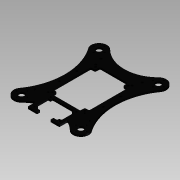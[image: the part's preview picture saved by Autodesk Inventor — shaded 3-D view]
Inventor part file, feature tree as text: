
AUTODESK INVENTOR PART (.ipt)
format: ipt  version: 2015 SP1 (Build 190203100, 203)  size: 542,208 bytes
history: native  units: mm
features: sketch x13, extrude x8, reference x2, projected_geometry x2
ambient origin geometry x8: Origin, YZ Plane, XZ Plane, XY Plane, X Axis, Y Axis, Z Axis, Center Point
bodies: Body1 (feature_tree)
feature tree (25):
  extrude  "Extrusion6"  Depth=9.0mm
  sketch  "Sketch5"  dims[d43=9.0mm d46=2.5mm]
  sketch  "Sketch7"  dims[d86=12.004481mm d87=6.00224mm]
  extrude  "Extrusion11"  Depth=2.5mm
  extrude  "Extrusion12"  Depth=6.00224mm
  sketch  "Sketch12"  dims[d95=5.821895mm d97=68.48mm]
  extrude  "Extrusion16"  Depth=69.254481mm
  extrude  "Extrusion17"  Depth=5.821895mm
  sketch  "Sketch16"  dims[d102=10.0mm]
  extrude  "Extrusion18"  Depth=68.48mm
  extrude  "Extrusion19"  Depth=9.0mm
  sketch  "Sketch18"  dims[d103=9.0mm]
  extrude  "Extrusion20"  Depth=2.5mm
  sketch  "Sketch20"  dims[d112=90.0deg]
  sketch  "Sketch21"  dims[d113=3.5mm d114=5.0mm d116=3.5mm d117=5.0mm d119=3.5mm d120=5.0mm d121=5.0mm d122=3.5mm d123=5.0mm d124=5.0mm d126=10.0mm d133=1.0mm d135=3.0mm d136=0.0mm d137=1.0mm d138=3.5mm d139=3.5mm d140=3.5mm d141=3.5mm d142=1.0mm d143=3.5mm d144=3.5mm d145=3.5mm d146=1.0mm d147=90.0deg d150=4.0mm d154=70.0mm d155=4.0mm d163=79.21229mm d164=117.809047mm d165=146.323167mm d166=3.5mm d167=0.0mm d170=146.323246mm d171=117.849958mm d172=3.0mm d173=0.0mm d181=146.323246mm d182=117.849958mm d183=3.5mm d186=40.0mm d187=37.5mm d190=90.0deg d194=10.0mm d195=0.0mm d198=43.0mm d199=85.0mm d200=43.0mm d201=85.0mm d202=10.0mm d203=0.0mm d204=3.0mm d205=0.0mm d206=0.0mm d207=0.0mm d208=30.222147mm d209=8.37276mm d210=26.980433mm d211=0.34724mm d212=3.0mm d213=0.0mm]
  sketch  "Sketch1"  dims[d26=29.0mm d42=9.0mm]
  sketch  "Sketch8"  dims[d88=6.00224mm d92=69.254481mm]
  sketch  "Sketch10"  dims[d93=27.79742mm d94=5.821895mm]
  sketch  "Sketch14"  dims[d98=51.000004mm d99=9.0mm]
  sketch  "Sketch15"  dims[d100=8.486696mm d101=2.5mm]
  reference  "Reference5"
  reference  "Reference6"
  sketch  "Sketch19"  dims[d104=8.486696mm]
  projected_geometry  "Projected Loop2"
  projected_geometry  "Projected Loop3"
